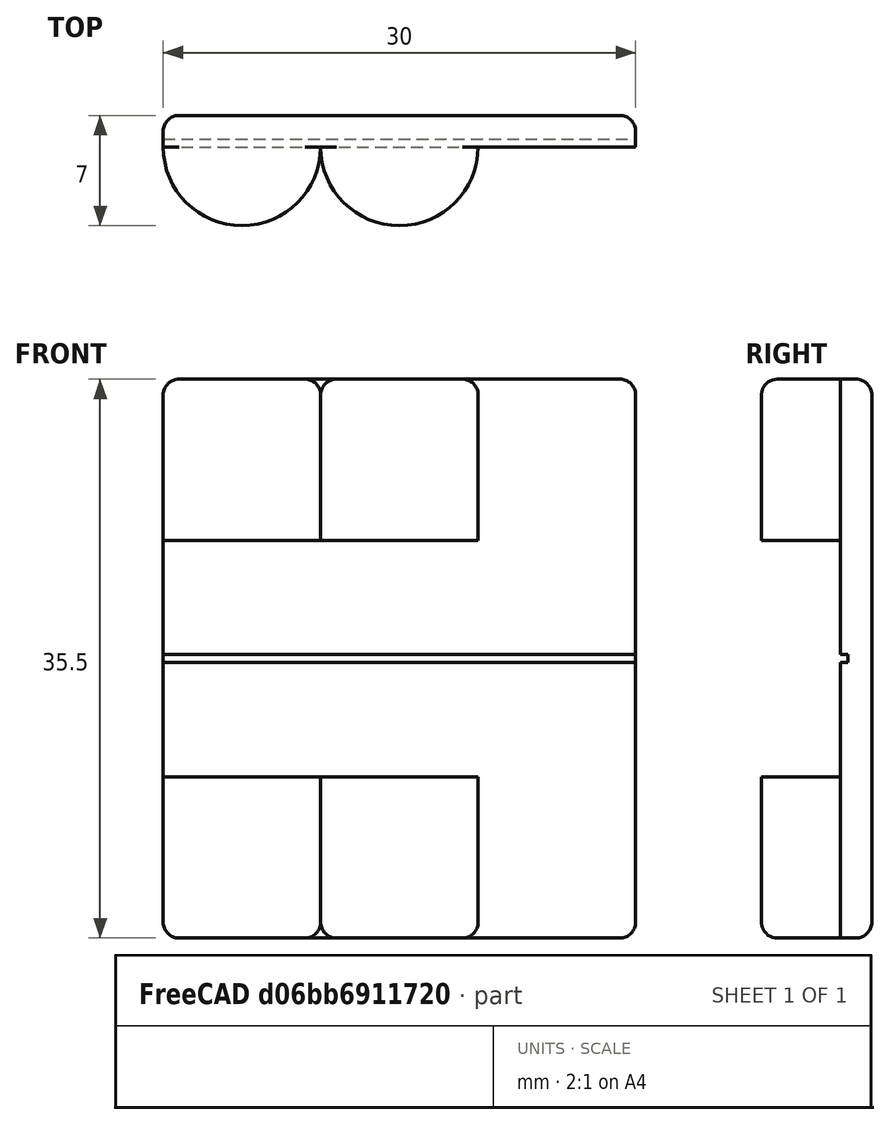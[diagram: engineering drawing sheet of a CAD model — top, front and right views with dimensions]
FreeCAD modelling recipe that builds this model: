
FCSTD DOCUMENT  (FreeCAD 0.16R6712 (Git))
Label: alignment jig 2 b
License: All rights reserved
LicenseURL: http://en.wikipedia.org/wiki/All_rights_reserved
objects: Part::Box×4, Part::Fillet×4, Part::Cylinder×2, Part::MultiFuse×2, Part::Cut×2
note: 14 computed .brp shape members not serialized (recipe doc carries the construction recipe); baked Part::Feature solids carry a one-line shape summary decoded from their .brp

FEATURE [Part::Cylinder] Cylinder
  Angle = 360
  Height = 35.5
  Placement = pos=(10,0,0) rot=(0,0,1;0rad)
  Radius = 5
FEATURE [Part::Cylinder] Cylinder001
  Angle = 360
  Height = 35.5
  Radius = 5
FEATURE [Part::Box] Box  label="Cube"
  Height = 35.5
  Length = 30
  Placement = pos=(-5,0,0) rot=(0,0,1;0rad)
  Width = 2.5
FEATURE [Part::Box] Box001  label="Cube001"
  Height = 35.5
  Length = 40
  Placement = pos=(-15,2,0) rot=(0,0,1;0rad)
  Width = 6
FEATURE [Part::Box] Box002  label="Cube002"
  Height = 15
  Length = 20
  Placement = pos=(-5,-5,10.25) rot=(0,0,1;0rad)
  Width = 5
FEATURE [Part::Box] Box003  label="Cube003"
  Height = 0.5
  Length = 50
  Placement = pos=(-18,-9.5,17.5) rot=(0,0,1;0rad)
  Width = 10
FEATURE [Part::MultiFuse] Fusion
  Shapes = -> [Box002,Box003]
FEATURE [Part::Fillet] Fillet
  Base = -> Cylinder
  Edges = 2 edges r=1: [Edge1,Edge3]
FEATURE [Part::Fillet] Fillet001
  Base = -> Cylinder001
  Edges = 2 edges r=1: [Edge1,Edge3]
FEATURE [Part::MultiFuse] Fusion001
  Shapes = -> [Box,Fillet,Fillet001]
FEATURE [Part::Cut] Cut
  Base = -> Fusion001
  Tool = -> Fusion
FEATURE [Part::Cut] Cut001
  Base = -> Cut
  Tool = -> Box001
FEATURE [Part::Fillet] Fillet002
  Base = -> Cut001
  Edges = 4 edges r=1: [Edge8,Edge14,Edge58,Edge59]
FEATURE [Part::Fillet] Fillet003
  Base = -> Fillet002
  Edges = 16 edges r=1: [Edge8,Edge12,Edge17,Edge31,Edge32,Edge33,Edge34,Edge35,Edge36,Edge37,Edge38,Edge39,Edge40,Edge41,Edge42,Edge43]
